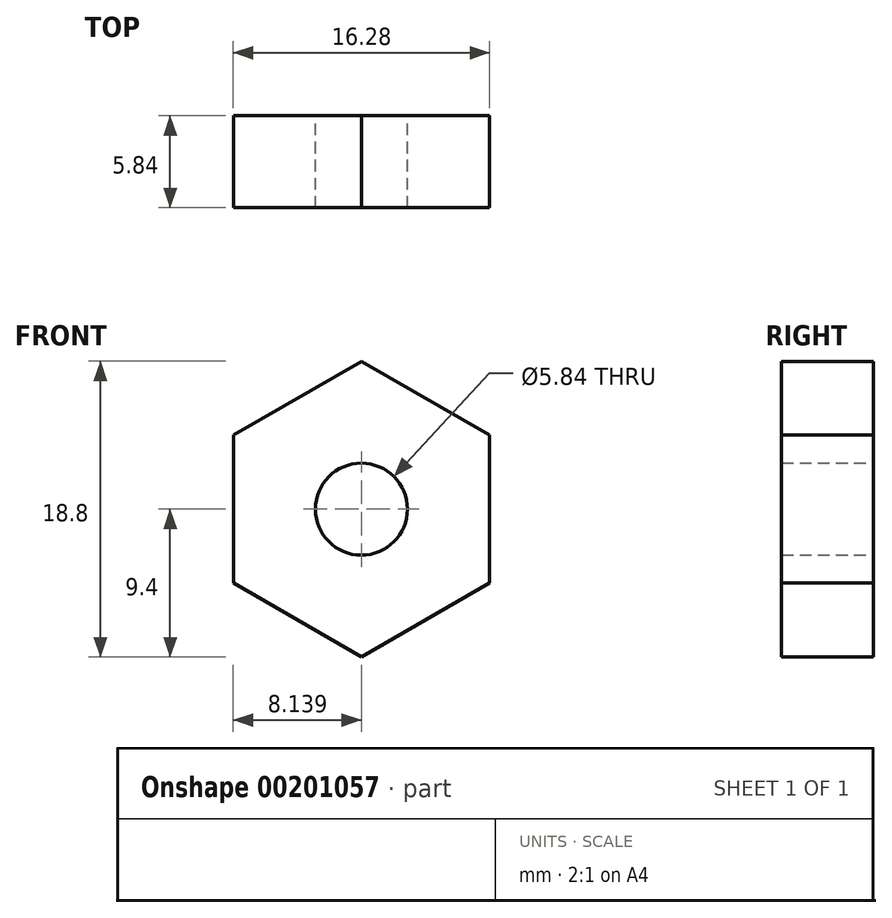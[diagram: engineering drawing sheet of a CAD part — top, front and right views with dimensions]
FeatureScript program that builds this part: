
annotation { "Feature Type Name" : "Feature", "Feature Type Description" : "" }
export const myFeature = defineFeature(function(context is Context, id is Id, definition is map)
    precondition{}
    {
        {
            var Q0;
            Q0=qCreatedBy(makeId("Front.planeOp"),FACE);
            var sketch = newSketch(context, id + "F0", { "sketchPlane" : qUnion([Q0])});
            skLineSegment(sketch, "E0.left", {"start": v(-50.81, 4.7) * mm, "end": v(-50.81, -4.74) * mm});
            skCircle(sketch, "E1.cCircle", {"center": v(-58.95, 0) * mm, "radius": 8.14 * mm, "construction": true});
            skLineSegment(sketch, "E1.1", {"start": v(-50.81, -4.7) * mm, "end": v(-58.95, -9.4) * mm});
            skLineSegment(sketch, "E1.2", {"start": v(-58.95, -9.4) * mm, "end": v(-67.09, -4.7) * mm});
            skLineSegment(sketch, "E1.3", {"start": v(-67.09, -4.7) * mm, "end": v(-67.09, 4.7) * mm});
            skLineSegment(sketch, "E1.4", {"start": v(-67.09, 4.7) * mm, "end": v(-58.95, 9.4) * mm});
            skLineSegment(sketch, "E1.5", {"start": v(-58.95, 9.4) * mm, "end": v(-50.81, 4.7) * mm});
            skPoint(sketch, "E1.0.midPoint", {"position": v(-50.81, 0) * mm});
            skCircle(sketch, "E2.MirrorC", {"center": v(58.95, 0) * mm, "radius": 8.14 * mm, "construction": true});
            skLineSegment(sketch, "E3.MirrorCS", {"start": v(50.81, -4.7) * mm, "end": v(58.95, -9.4) * mm});
            skLineSegment(sketch, "E4.MirrorCS", {"start": v(50.81, 4.7) * mm, "end": v(50.81, -4.7) * mm});
            skLineSegment(sketch, "E5.MirrorCS", {"start": v(58.95, 9.4) * mm, "end": v(50.81, 4.7) * mm});
            skLineSegment(sketch, "E6.MirrorCS", {"start": v(67.09, 4.7) * mm, "end": v(58.95, 9.4) * mm});
            skLineSegment(sketch, "E7.MirrorCS", {"start": v(67.09, -4.7) * mm, "end": v(67.09, 4.7) * mm});
            skLineSegment(sketch, "E8.MirrorCS", {"start": v(58.95, -9.4) * mm, "end": v(67.09, -4.7) * mm});
            skLineSegment(sketch, "E9.bottom", {"start": v(-50.81, 4.7) * mm, "end": v(50.81, 4.7) * mm});
            skLineSegment(sketch, "E9.top", {"start": v(-50.81, -4.7) * mm, "end": v(50.81, -4.7) * mm});
            skLineSegment(sketch, "E9.left", {"start": v(-50.81, 4.7) * mm, "end": v(-50.81, -4.7) * mm});
            skPoint(sketch, "E9.middle", {"position": v(0, 0) * mm});
            skSolve(sketch);
        }
        {
            var Q0;
            Q0=makeQuery(id+"F0.imprint","IMPRINT",FACE,{"disambiguationData":[TD([[makeQuery(id+"F0.imprint","IMPRINT",EDGE,{"derivedFrom":sQuery(id+"F0.wireOp",EDGE,"E1.0")}),1.0]])]});
            var Q1;
            Q1=makeQuery(id+"F0.imprint","IMPRINT",FACE,{"disambiguationData":[TD([[makeQuery(id+"F0.imprint","IMPRINT",EDGE,{"derivedFrom":sQuery(id+"F0.wireOp",EDGE,"E1.0")}),-1.0]])]});
            var Q2;
            Q2=makeQuery(id+"F0.imprint","IMPRINT",FACE,{"disambiguationData":[TD([[makeQuery(id+"F0.imprint","IMPRINT",EDGE,{"derivedFrom":sQuery(id+"F0.wireOp",EDGE,"E3.MirrorCS")}),1.0]])]});
            extrude(context, id + "F1", {"entities" : qUnion([Q0, Q1, Q2]), "depth" : 5.84 * mm});
        }
        {
            var Q0;
            Q0=sQuery(id+"F0.wireOp",VERTEX,"E2.MirrorC.center");
            var Q1;
            Q1=makeQuery(id+"F1.opExtrude","SWEPT_BODY",BODY,{"disambiguationData":[OSD([sQuery(id+"F0.wireOp",EDGE,"E1.1"),sQuery(id+"F0.wireOp",EDGE,"E1.2"),sQuery(id+"F0.wireOp",EDGE,"E1.3"),sQuery(id+"F0.wireOp",EDGE,"E1.4"),sQuery(id+"F0.wireOp",EDGE,"E1.5"),sQuery(id+"F0.wireOp",EDGE,"E3.MirrorCS"),sQuery(id+"F0.wireOp",EDGE,"E5.MirrorCS"),sQuery(id+"F0.wireOp",EDGE,"E6.MirrorCS"),sQuery(id+"F0.wireOp",EDGE,"E7.MirrorCS"),sQuery(id+"F0.wireOp",EDGE,"E8.MirrorCS"),sQuery(id+"F0.wireOp",EDGE,"DaViUEyd-yUje-YU1W-p1GX-GPF2h4ZRjxqC"),sQuery(id+"F0.wireOp",EDGE,"jAGTVoY8-qRZz-QGgt-63u2-20EiAg8DRz1O")])]});
            hole(context, id + "F2", {"style" : HoleStyle.SIMPLE, "endStyle" : HoleEndStyle.THROUGH, "oppositeDirection" : true, "holeDiameter" : 5.84 * mm, "locations" : qUnion([Q0]), "scope" : qUnion([Q1]), "isTappedThrough" : true});
        }
    });
